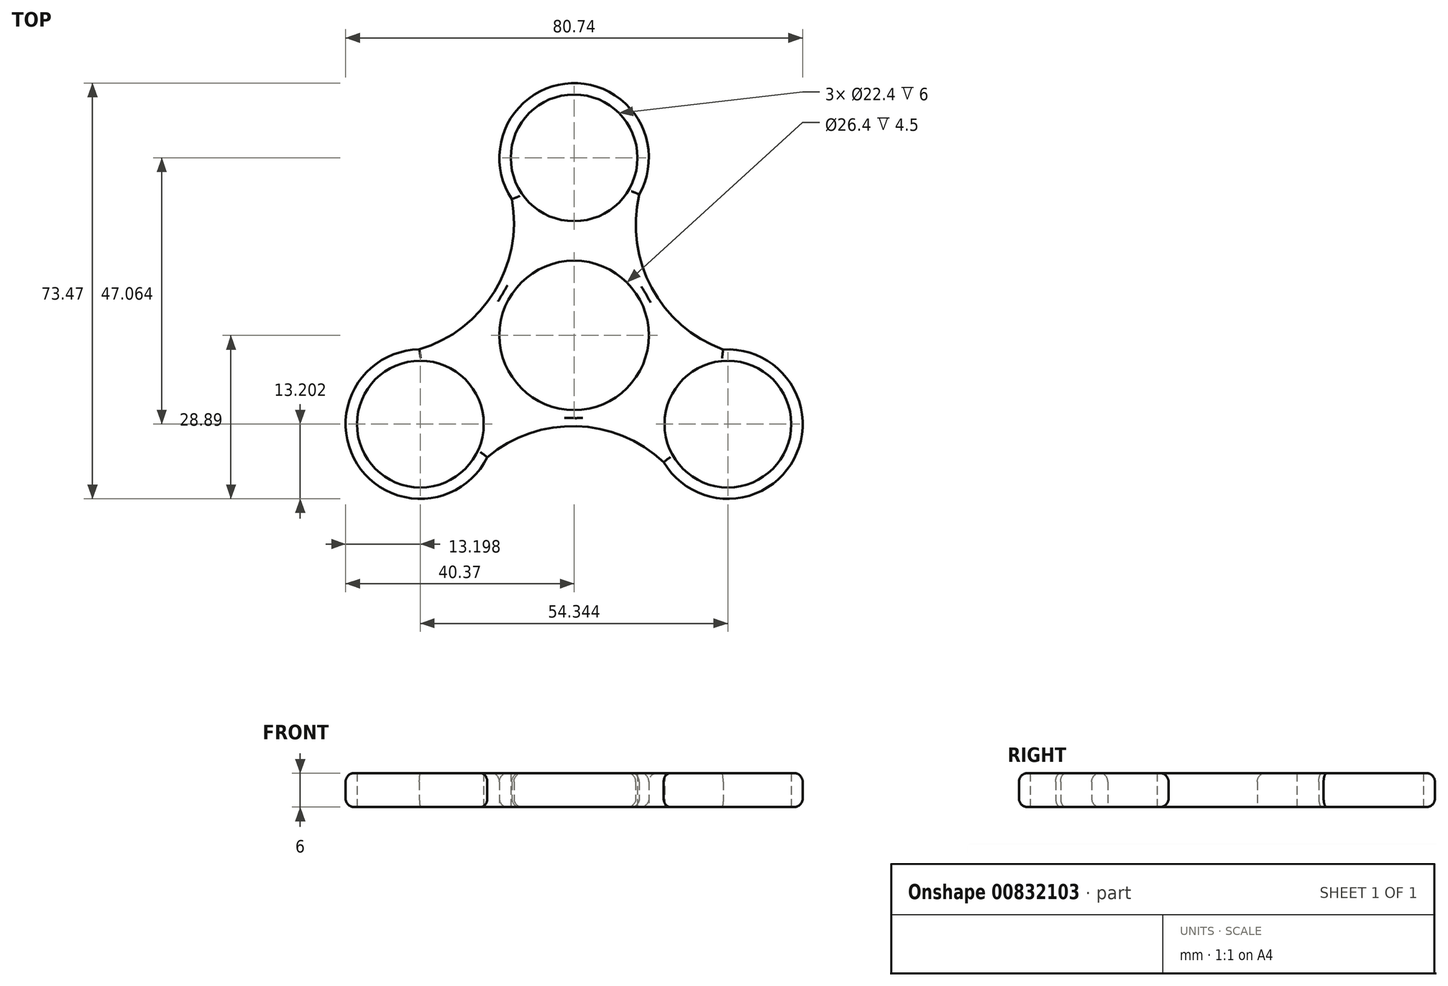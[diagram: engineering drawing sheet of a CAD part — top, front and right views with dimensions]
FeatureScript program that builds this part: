
annotation { "Feature Type Name" : "Feature", "Feature Type Description" : "" }
export const myFeature = defineFeature(function(context is Context, id is Id, definition is map)
    precondition{}
    {
        {
            var Q0;
            Q0=qCreatedBy(makeId("Top.planeOp"),FACE);
            var sketch = newSketch(context, id + "F0", { "sketchPlane" : qUnion([Q0])});
            skCircle(sketch, "E0", {"center": v(0, 0) * mm, "radius": 11.2 * mm});
            skCircle(sketch, "E1", {"center": v(0, 0) * mm, "radius": 13.2 * mm});
            skCircle(sketch, "E2", {"center": v(0, 31.38) * mm, "radius": 11.2 * mm});
            skCircle(sketch, "E3", {"center": v(0, 31.38) * mm, "radius": 13.2 * mm});
            skCircle(sketch, "E4.1.0", {"center": v(-27.17, -15.69) * mm, "radius": 11.2 * mm});
            skCircle(sketch, "E4.1.1", {"center": v(-27.17, -15.69) * mm, "radius": 13.2 * mm});
            skCircle(sketch, "E4.2.0", {"center": v(27.17, -15.69) * mm, "radius": 11.2 * mm});
            skCircle(sketch, "E4.2.1", {"center": v(27.17, -15.69) * mm, "radius": 13.2 * mm});
            skLineSegment(sketch, "E5", {"start": v(5.6, 21.68) * mm, "end": v(6.6, 19.94) * mm, "construction": true});
            skLineSegment(sketch, "E6", {"start": v(-17.47, -10.09) * mm, "end": v(-15.74, -9.09) * mm, "construction": true});
            skArc(sketch, "E7", {"start": v(11.51, 24.92) * mm, "mid": v(13.7, 8.38) * mm, "end": v(26.34, -2.51) * mm});
            skArc(sketch, "E8.1.0", {"start": v(-27.34, -2.49) * mm, "mid": v(-14.11, 7.68) * mm, "end": v(-11, 24.06) * mm});
            skArc(sketch, "E8.2.0", {"start": v(15.83, -22.43) * mm, "mid": v(0.4, -16.06) * mm, "end": v(-15.35, -21.55) * mm});
            skLineSegment(sketch, "E9.trimOffspring", {"start": v(20.57, -4.26) * mm, "end": v(21.57, -5.99) * mm, "construction": true});
            skLineSegment(sketch, "E10.trimOffspring", {"start": v(9.7, 5.6) * mm, "end": v(11.43, 6.6) * mm, "construction": true});
            skLineSegment(sketch, "E11.trimOffspring", {"start": v(-11.43, -6.6) * mm, "end": v(-9.7, -5.6) * mm, "construction": true});
            skSolve(sketch);
        }
        {
            var Q0;
            Q0 = qSketchRegion(id + "F0", true);
            extrude(context, id + "F1", {"entities" : qUnion([Q0]), "depth" : 6 * mm, "offsetDistance" : 25 * mm});
        }
        {
            var Q0;
            Q0=makeQuery(id+"F1.opExtrude","CAP_EDGE",EDGE,{"disambiguationData":[OSD([sQuery(id+"F0.wireOp",EDGE,"E4.1.1")])],"isStart":false});
            var Q1;
            Q1=makeQuery(id+"F1.opExtrude","CAP_EDGE",EDGE,{"disambiguationData":[OSD([sQuery(id+"F0.wireOp",EDGE,"E8.2.0")])],"isStart":false});
            var Q2;
            Q2=makeQuery(id+"F1.opExtrude","CAP_EDGE",EDGE,{"disambiguationData":[OSD([sQuery(id+"F0.wireOp",EDGE,"E4.2.1")])],"isStart":false});
            var Q3;
            Q3=makeQuery(id+"F1.opExtrude","CAP_EDGE",EDGE,{"disambiguationData":[OSD([sQuery(id+"F0.wireOp",EDGE,"E1")])],"isStart":false});
            var Q4;
            Q4=makeQuery(id+"F1.opExtrude","CAP_EDGE",EDGE,{"disambiguationData":[OSD([sQuery(id+"F0.wireOp",EDGE,"E3")])],"isStart":false});
            var Q5;
            Q5=makeQuery(id+"F1.opExtrude","CAP_EDGE",EDGE,{"disambiguationData":[OSD([sQuery(id+"F0.wireOp",EDGE,"E8.1.0")])],"isStart":false});
            var Q6;
            Q6=makeQuery(id+"F1.opExtrude","CAP_EDGE",EDGE,{"disambiguationData":[OSD([sQuery(id+"F0.wireOp",EDGE,"E7")])],"isStart":false});
            fillet(context, id + "F2", {"entities" : qUnion([Q0, Q1, Q2, Q3, Q4, Q5, Q6]), "radius" : 1.5 * mm, "tangentPropagation" : true, "allowEdgeOverflow" : false});
        }
        {
            var Q0;
            Q0=makeQuery(id+"F1.opExtrude","CAP_EDGE",EDGE,{"disambiguationData":[OSD([sQuery(id+"F0.wireOp",EDGE,"E4.1.1")])],"isStart":true});
            var Q1;
            Q1=makeQuery(id+"F1.opExtrude","CAP_EDGE",EDGE,{"disambiguationData":[OSD([sQuery(id+"F0.wireOp",EDGE,"E8.2.0")])],"isStart":true});
            var Q2;
            Q2=makeQuery(id+"F1.opExtrude","CAP_EDGE",EDGE,{"disambiguationData":[OSD([sQuery(id+"F0.wireOp",EDGE,"E4.2.1")])],"isStart":true});
            var Q3;
            Q3=makeQuery(id+"F1.opExtrude","CAP_EDGE",EDGE,{"disambiguationData":[OSD([sQuery(id+"F0.wireOp",EDGE,"E7")])],"isStart":true});
            var Q4;
            Q4=makeQuery(id+"F1.opExtrude","CAP_EDGE",EDGE,{"disambiguationData":[OSD([sQuery(id+"F0.wireOp",EDGE,"E3")])],"isStart":true});
            var Q5;
            Q5=makeQuery(id+"F1.opExtrude","CAP_EDGE",EDGE,{"disambiguationData":[OSD([sQuery(id+"F0.wireOp",EDGE,"E8.1.0")])],"isStart":true});
            fillet(context, id + "F3", {"entities" : qUnion([Q0, Q1, Q2, Q3, Q4, Q5]), "radius" : 1.5 * mm, "tangentPropagation" : true, "allowEdgeOverflow" : false});
        }
    });
